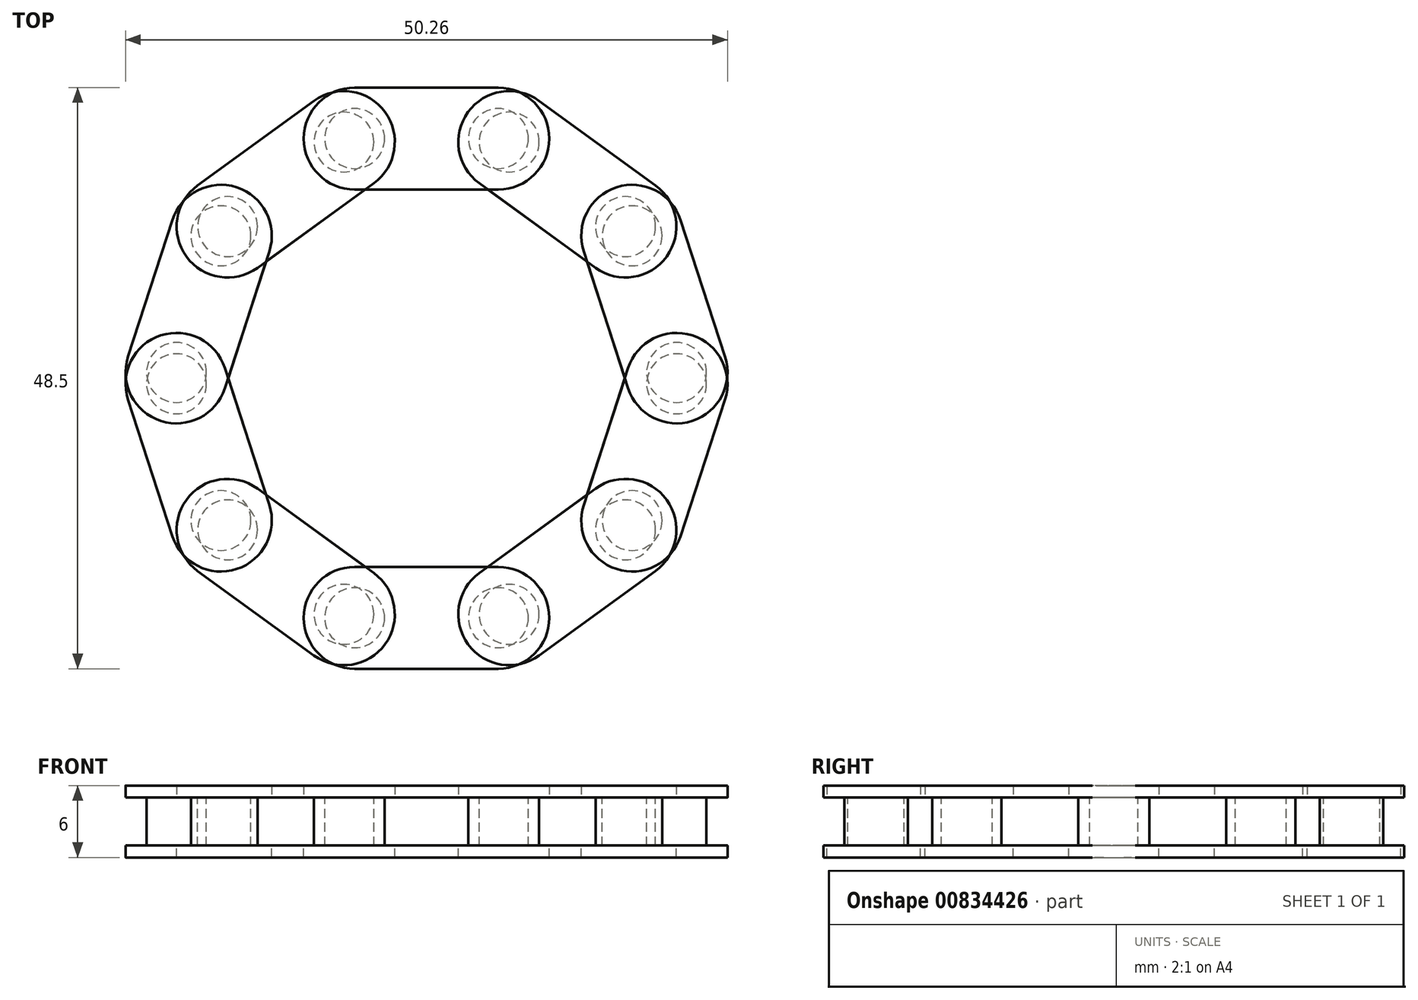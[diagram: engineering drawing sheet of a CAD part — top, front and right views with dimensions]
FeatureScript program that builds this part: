
annotation { "Feature Type Name" : "Feature", "Feature Type Description" : "" }
export const myFeature = defineFeature(function(context is Context, id is Id, definition is map)
    precondition{}
    {
        {
            var Q0;
            Q0=qCreatedBy(makeId("Top.planeOp"),FACE);
            var sketch = newSketch(context, id + "F0", { "sketchPlane" : qUnion([Q0])});
            skLineSegment(sketch, "E0", {"start": v(-6, -4.25) * mm, "end": v(6, -4.25) * mm});
            skLineSegment(sketch, "E1", {"start": v(-6, 4.25) * mm, "end": v(6, 4.25) * mm});
            skArc(sketch, "E2", {"start": v(-6, 4.25) * mm, "mid": v(-10.25, 0) * mm, "end": v(-6, -4.25) * mm});
            skArc(sketch, "E3", {"start": v(6, -4.25) * mm, "mid": v(10.25, 0) * mm, "end": v(6, 4.25) * mm});
            skPoint(sketch, "E4", {"position": v(0, 4.25) * mm});
            skCircle(sketch, "E5", {"center": v(-6, 0) * mm, "radius": 2.5 * mm});
            skCircle(sketch, "E6", {"center": v(6, 0) * mm, "radius": 2.5 * mm});
            skSolve(sketch);
        }
        {
            var Q0;
            Q0=makeQuery(id+"F0.imprint","IMPRINT",FACE,{"disambiguationData":[TD([[makeQuery(id+"F0.imprint","IMPRINT",EDGE,{"derivedFrom":sQuery(id+"F0.wireOp",EDGE,"E0")}),1.0]])]});
            var Q1;
            {var subQ0=sQuery(id+"F0.wireOp",EDGE,"XDQfHUuL-DFFx-psEM-iLCj-taBEPvJks0z6");var subQ1=makeQuery(id+"F0.imprint","INTERSECT",VERTEX,{"derivedFrom":[sQuery(id+"F0.wireOp",EDGE,"E0"),subQ0]});Q1=makeQuery(id+"F0.imprint","IMPRINT",FACE,{"disambiguationData":[TD([[makeQuery(id+"F0.imprint","IMPRINT",EDGE,{"disambiguationData":[TD([[subQ1,1.0]])],"derivedFrom":subQ0}),1.0]])]});}
            var Q2;
            {var subQ0=sQuery(id+"F0.wireOp",EDGE,"5DUu5umR-uthN-ov28-ysG1-g1TjbopaZGNy");var subQ1=makeQuery(id+"F0.imprint","INTERSECT",VERTEX,{"derivedFrom":[sQuery(id+"F0.wireOp",EDGE,"E0"),subQ0]});Q2=makeQuery(id+"F0.imprint","IMPRINT",FACE,{"disambiguationData":[TD([[makeQuery(id+"F0.imprint","IMPRINT",EDGE,{"disambiguationData":[TD([[subQ1,1.0]])],"derivedFrom":subQ0}),1.0]])]});}
            var Q3;
            Q3=makeQuery(id+"F0.imprint","IMPRINT",FACE,{"disambiguationData":[TD([[makeQuery(id+"F0.imprint","IMPRINT",EDGE,{"derivedFrom":sQuery(id+"F0.wireOp",EDGE,"E5")}),1.0]])]});
            var Q4;
            Q4=makeQuery(id+"F0.imprint","IMPRINT",FACE,{"disambiguationData":[TD([[makeQuery(id+"F0.imprint","IMPRINT",EDGE,{"derivedFrom":sQuery(id+"F0.wireOp",EDGE,"E6")}),1.0]])]});
            extrude(context, id + "F1", {"entities" : qUnion([Q0, Q1, Q2, Q3, Q4]), "depth" : 1 * mm, "offsetDistance" : 25 * mm});
        }
        {
            var Q0;
            Q0=makeQuery(id+"F0.imprint","IMPRINT",FACE,{"disambiguationData":[TD([[makeQuery(id+"F0.imprint","IMPRINT",EDGE,{"derivedFrom":sQuery(id+"F0.wireOp",EDGE,"E5")}),1.0]])]});
            var Q1;
            Q1=makeQuery(id+"F0.imprint","IMPRINT",FACE,{"disambiguationData":[TD([[makeQuery(id+"F0.imprint","IMPRINT",EDGE,{"derivedFrom":sQuery(id+"F0.wireOp",EDGE,"E6")}),1.0]])]});
            extrude(context, id + "F2", {"entities" : qUnion([Q0, Q1]), "operationType" : NewBodyOperationType.ADD, "oppositeDirection" : true, "depth" : 4 * mm, "offsetDistance" : 25 * mm});
        }
        {
            var Q0;
            Q0=makeQuery(id+"F2.opExtrude","CAP_FACE",FACE,{"disambiguationData":[OSD([sQuery(id+"F0.wireOp",EDGE,"E5")])],"isStart":false});
            var sketch = newSketch(context, id + "F3", { "sketchPlane" : qUnion([Q0])});
            skLineSegment(sketch, "E7", {"start": v(-6, -4.25) * mm, "end": v(6, -4.25) * mm});
            skLineSegment(sketch, "E8.MirrorCS", {"start": v(-6, 4.25) * mm, "end": v(6, 4.25) * mm});
            skArc(sketch, "E9", {"start": v(-6, 4.25) * mm, "mid": v(-10.25, 0) * mm, "end": v(-6, -4.25) * mm});
            skArc(sketch, "E10.MirrorCS", {"start": v(6, 4.25) * mm, "mid": v(10.25, 0) * mm, "end": v(6, -4.25) * mm});
            skSolve(sketch);
        }
        {
            var Q0;
            Q0=makeQuery(id+"F3.imprint","IMPRINT",FACE,{"disambiguationData":[TD([[makeQuery(id+"F3.imprint","IMPRINT",EDGE,{"derivedFrom":makeQuery(id+"F2.opExtrude","CAP_EDGE",EDGE,{"disambiguationData":[OSD([sQuery(id+"F0.wireOp",EDGE,"E5")])],"isStart":false})}),-1.0]])]});
            var Q1;
            Q1=makeQuery(id+"F3.imprint","IMPRINT",FACE,{"disambiguationData":[TD([[makeQuery(id+"F3.imprint","IMPRINT",EDGE,{"derivedFrom":sQuery(id+"F3.wireOp",EDGE,"E7")}),1.0]])]});
            extrude(context, id + "F4", {"entities" : qUnion([Q0, Q1]), "operationType" : NewBodyOperationType.ADD, "depth" : 1 * mm, "offsetDistance" : 25 * mm});
        }
        {
            var Q0;
            Q0=qCreatedBy(makeId("Top.planeOp"),FACE);
            var sketch = newSketch(context, id + "F5", { "sketchPlane" : qUnion([Q0])});
            skCircle(sketch, "E11", {"center": v(0, -20) * mm, "radius": 20 * mm});
            skSolve(sketch);
        }
        {
            var Q0;
            Q0=makeQuery(id+"F1.opExtrude","SWEPT_BODY",BODY,{"disambiguationData":[OSD([sQuery(id+"F0.wireOp",EDGE,"E0"),sQuery(id+"F0.wireOp",EDGE,"E1"),sQuery(id+"F0.wireOp",EDGE,"E2"),sQuery(id+"F0.wireOp",EDGE,"E3")])]});
            var Q1;
            Q1=sQuery(id+"F5.wireOp",EDGE,"E11");
            circularPattern(context, id + "F6", {"entities" : qUnion([Q0]), "axis" : qUnion([Q1]), "angle" : 360 * degree, "instanceCount" : 10, "equalSpace" : true});
        }
    });
